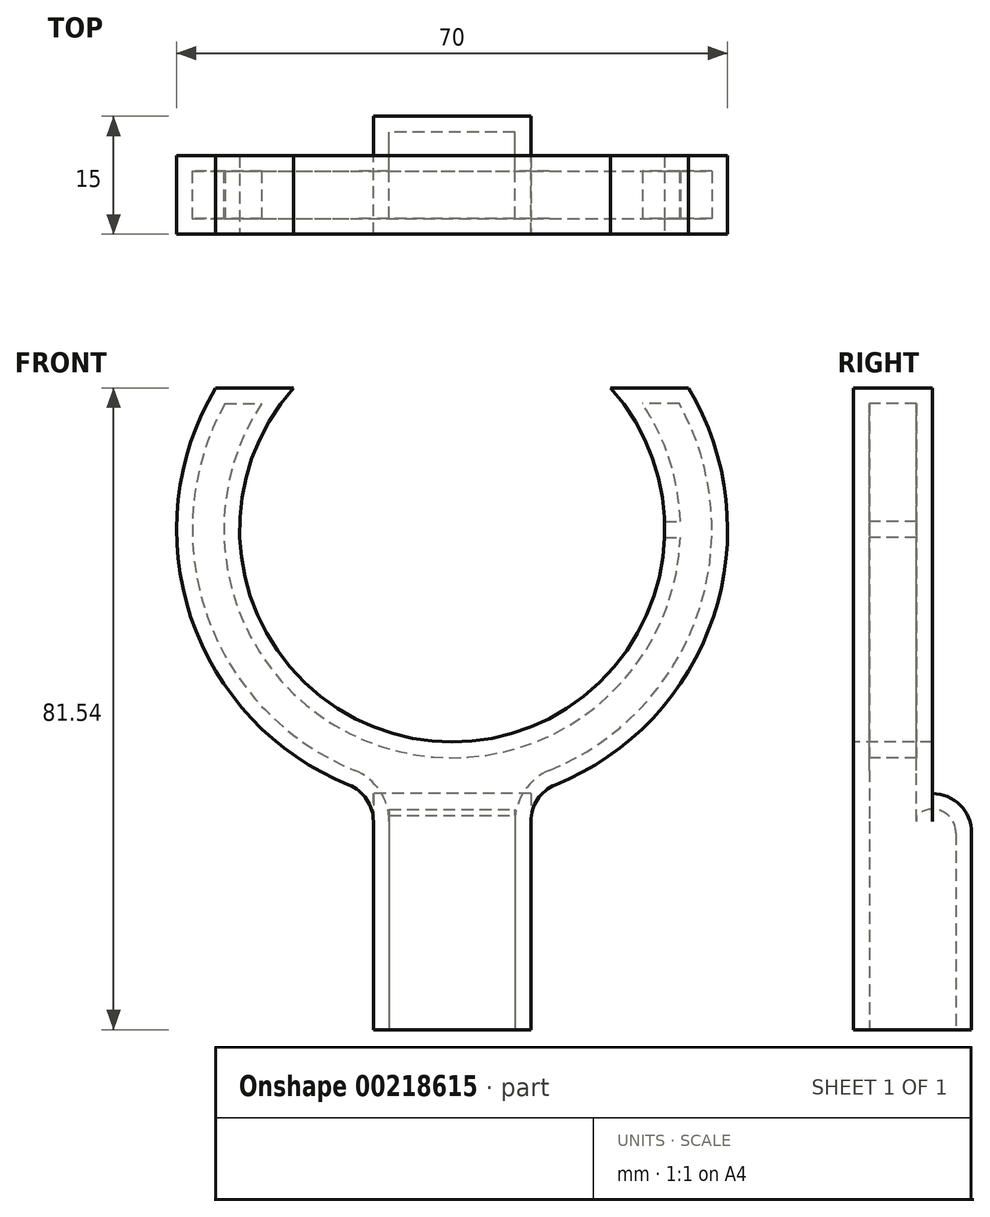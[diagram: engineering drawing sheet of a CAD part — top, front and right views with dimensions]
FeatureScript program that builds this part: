
annotation { "Feature Type Name" : "Feature", "Feature Type Description" : "" }
export const myFeature = defineFeature(function(context is Context, id is Id, definition is map)
    precondition{}
    {
        {
            var Q0;
            Q0=qCreatedBy(makeId("Top.planeOp"),FACE);
            var sketch = newSketch(context, id + "F0", { "sketchPlane" : qUnion([Q0])});
            skLineSegment(sketch, "E0.bottom", {"start": v(10, -7.5) * mm, "end": v(-10, -7.5) * mm});
            skLineSegment(sketch, "E0.top", {"start": v(10, 7.5) * mm, "end": v(-10, 7.5) * mm});
            skLineSegment(sketch, "E0.left", {"start": v(10, -7.5) * mm, "end": v(10, 7.5) * mm});
            skLineSegment(sketch, "E0.right", {"start": v(-10, -7.5) * mm, "end": v(-10, 7.5) * mm});
            skPoint(sketch, "E0.middle", {"position": v(0, 0) * mm});
            skSolve(sketch);
        }
        {
            var Q0;
            Q0 = qSketchRegion(id + "F0", true);
            extrude(context, id + "F1", {"entities" : qUnion([Q0]), "depth" : 30 * mm, "offsetDistance" : 25 * mm});
        }
        {
            var Q0;
            Q0=makeQuery(id+"F1.opExtrude","SWEPT_FACE",FACE,{"disambiguationData":[OSD([sQuery(id+"F0.wireOp",EDGE,"E0.bottom")])]});
            var sketch = newSketch(context, id + "F2", { "sketchPlane" : qUnion([Q0])});
            skArc(sketch, "E1", {"start": v(10, 30) * mm, "mid": v(32.63, 50.87) * mm, "end": v(30.02, 81.54) * mm});
            skArc(sketch, "E2.0", {"start": v(0, 36.54) * mm, "mid": v(24.65, 52.52) * mm, "end": v(20.12, 81.54) * mm});
            skLineSegment(sketch, "E3", {"start": v(0, 30) * mm, "end": v(0, 36.54) * mm, "construction": true});
            skLineSegment(sketch, "E4", {"start": v(-14.75, 36.54) * mm, "end": v(0, 36.54) * mm, "construction": true});
            skLineSegment(sketch, "E5", {"start": v(30.02, 81.54) * mm, "end": v(20.12, 81.54) * mm});
            skLineSegment(sketch, "E6.MirrorCS", {"start": v(-30.02, 81.54) * mm, "end": v(-20.12, 81.54) * mm});
            skArc(sketch, "E7.MirrorCS", {"start": v(-10, 30) * mm, "mid": v(-32.63, 50.87) * mm, "end": v(-30.02, 81.54) * mm});
            skArc(sketch, "E8.MirrorCS", {"start": v(0, 36.54) * mm, "mid": v(-24.65, 52.52) * mm, "end": v(-20.12, 81.54) * mm});
            skLineSegment(sketch, "E9", {"start": v(10, 30) * mm, "end": v(-10, 30) * mm});
            skSolve(sketch);
        }
        {
            var Q0;
            Q0 = qSketchRegion(id + "F2", true);
            extrude(context, id + "F3", {"entities" : qUnion([Q0]), "operationType" : NewBodyOperationType.ADD, "oppositeDirection" : true, "depth" : 10 * mm, "offsetDistance" : 25 * mm});
        }
        {
            var Q0;
            {var subQ0=sQuery(id+"F0.wireOp",EDGE,"E0.right");Q0=makeQuery(id+"F3.boolean.opBoolean","MERGE",EDGE,{"derivedFrom":[makeQuery(id+"F1.opExtrude","CAP_EDGE",EDGE,{"disambiguationData":[OSD([subQ0])],"isStart":false}),makeQuery(id+"F3.opExtrude","SWEPT_EDGE",EDGE,{"disambiguationData":[OSD([sQuery(id+"F0.wireOp",EDGE,"E0.bottom"),subQ0,sQuery(id+"F2.wireOp",EDGE,"E7.MirrorCS"),sQuery(id+"F2.wireOp",EDGE,"E9")])]})]});}
            var Q1;
            {var subQ0=sQuery(id+"F0.wireOp",EDGE,"E0.left");Q1=makeQuery(id+"F3.boolean.opBoolean","MERGE",EDGE,{"derivedFrom":[makeQuery(id+"F1.opExtrude","CAP_EDGE",EDGE,{"disambiguationData":[OSD([subQ0])],"isStart":false}),makeQuery(id+"F3.opExtrude","SWEPT_EDGE",EDGE,{"disambiguationData":[OSD([sQuery(id+"F0.wireOp",EDGE,"E0.bottom"),subQ0,sQuery(id+"F2.wireOp",EDGE,"E1"),sQuery(id+"F2.wireOp",EDGE,"E9")])]})]});}
            var Q2;
            Q2=makeQuery(id+"F3.opExtrude","CAP_EDGE",EDGE,{"disambiguationData":[OSD([sQuery(id+"F2.wireOp",EDGE,"E9")])],"isStart":false});
            var Q3;
            Q3=makeQuery(id+"F1.opExtrude","CAP_EDGE",EDGE,{"disambiguationData":[OSD([sQuery(id+"F0.wireOp",EDGE,"E0.top")])],"isStart":false});
            fillet(context, id + "F4", {"entities" : qUnion([Q0, Q1, Q2, Q3]), "tangentPropagation" : true, "radius" : 5 * mm, "defaultsChanged" : false, "vertexSettings" : [], "allowEdgeOverflow" : false});
        }
        {
            var Q0;
            Q0=makeQuery(id+"F1.opExtrude","CAP_FACE",FACE,{"disambiguationData":[OSD([sQuery(id+"F0.wireOp",EDGE,"E0.bottom"),sQuery(id+"F0.wireOp",EDGE,"E0.top"),sQuery(id+"F0.wireOp",EDGE,"E0.left"),sQuery(id+"F0.wireOp",EDGE,"E0.right")])],"isStart":true});
            shell(context, id + "F5", {"entities" : qUnion([Q0]), "thickness" : 2 * mm});
        }
        {
            var Q0;
            Q0=makeQuery(id+"F3.opExtrude","CAP_FACE",FACE,{"disambiguationData":[OSD([sQuery(id+"F2.wireOp",EDGE,"E1"),sQuery(id+"F2.wireOp",EDGE,"E2.0"),sQuery(id+"F2.wireOp",EDGE,"E5"),sQuery(id+"F2.wireOp",EDGE,"E6.MirrorCS"),sQuery(id+"F2.wireOp",EDGE,"E7.MirrorCS"),sQuery(id+"F2.wireOp",EDGE,"E8.MirrorCS"),sQuery(id+"F2.wireOp",EDGE,"E9")])],"isStart":false});
            var Q1;
            Q1=makeQuery(id+"F3.boolean.opBoolean","MERGE",FACE,{"derivedFrom":[makeQuery(id+"F1.opExtrude","SWEPT_FACE",FACE,{"disambiguationData":[OSD([sQuery(id+"F0.wireOp",EDGE,"E0.bottom")])]}),makeQuery(id+"F3.opExtrude","CAP_FACE",FACE,{"disambiguationData":[OSD([sQuery(id+"F2.wireOp",EDGE,"E1"),sQuery(id+"F2.wireOp",EDGE,"E2.0"),sQuery(id+"F2.wireOp",EDGE,"E5"),sQuery(id+"F2.wireOp",EDGE,"E6.MirrorCS"),sQuery(id+"F2.wireOp",EDGE,"E7.MirrorCS"),sQuery(id+"F2.wireOp",EDGE,"E8.MirrorCS"),sQuery(id+"F2.wireOp",EDGE,"E9")])],"isStart":true})]});
            cPlane(context, id + "F6", {"entities" : qUnion([Q0, Q1]), "cplaneType" : CPlaneType.MID_PLANE, "offset" : 25 * mm, "width" : 150 * mm, "height" : 150 * mm});
        }
        {
            var Q0;
            Q0=qCreatedBy(id+"F6.planeOp",FACE);
            var sketch = newSketch(context, id + "F7", { "sketchPlane" : qUnion([Q0])});
            skLineSegment(sketch, "E10.bottom", {"start": v(-24.5, 62.54) * mm, "end": v(-29.5, 62.54) * mm});
            skLineSegment(sketch, "E10.top", {"start": v(-24.5, 64.54) * mm, "end": v(-29.5, 64.54) * mm});
            skLineSegment(sketch, "E10.left", {"start": v(-24.5, 62.54) * mm, "end": v(-24.5, 64.54) * mm});
            skLineSegment(sketch, "E10.right", {"start": v(-29.5, 62.54) * mm, "end": v(-29.5, 64.54) * mm});
            skPoint(sketch, "E10.middle", {"position": v(-27, 63.54) * mm});
            skArc(sketch, "E11.0", {"start": v(20.12, 81.54) * mm, "mid": v(0, 36.54) * mm, "end": v(-20.12, 81.54) * mm, "construction": true});
            skSolve(sketch);
        }
        {
            var Q0;
            Q0 = qSketchRegion(id + "F7", true);
            extrude(context, id + "F8", {"entities" : qUnion([Q0]), "operationType" : NewBodyOperationType.REMOVE, "oppositeDirection" : true, "depth" : 6 * mm, "offsetDistance" : 25 * mm, "symmetric" : true});
        }
    });
